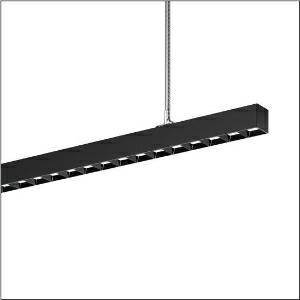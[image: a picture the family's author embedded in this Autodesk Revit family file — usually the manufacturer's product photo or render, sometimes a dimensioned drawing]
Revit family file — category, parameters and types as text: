
# Revit family: silica_r__21_51mx32dc4dbb_b922
name_source: partatom
category: Lighting Fixtures
units: mm (PartAtom-declared; Revit-internal decimal feet)

## family parameters
Cut with Voids When Loaded = No
Host = Face
Light Source = No
Part Type = Normal
Room Calculation Point = No
Round Connector Dimension = Use Diameter
Shared = No

## types (1)
- --- (1 x LED, 18230 lm, 105.8 W, 4000K)
    Apparent Load = 106 VA
    CIE Flux Codes = 86 99 100 59 100
    Color Rendering = 80
    Color Temperature = 4000K
    Default Elevation = 1800 mm
    Description = Silica® 21, office luminaire, primary light control with darklight reflector, of PMMA, black, CAT 2 (L<= 3000cd/m²), light emission: direct/indirect distribution, primary light characteristic: symmetric, installation type: suspended mounting, LED, rated luminous flux: 18.230lm, luminous efficacy: 172lm/W, light colour: 840, colour temperature: 4000K, control gear: DALI 2, with terminal, 3+2-pole, max. 2.5mm², mains connection: 220..240V, AC, 50/60Hz, rated input power: 105.8W, luminaire housing, of aluminium, matt jet black (RAL 9005), length: 3.004mm, width: 53mm, height: 53mm, protection rating (complete): IP20, insulation class (complete): insulation class I (protective earthing), certification: CE, permissible operating ambient temperature: 0..+35°C, standard: EN 50419, packaging unit: 1 piece
    Height = 53 mm
    Lamp = 1 x LED
    Lamp Light Flux = 18230 lm
    Lamp Power = 105.8 W
    Lamp count = 1
    Length = 3004 mm
    Luminous efficacy = 172 lm/W
    Manufacturer = Siteco
    ModVariant = No
    Model = 51MX32DC4DBB
    Mounting Place = Ceiling
    Mounting Type = Pendant
    Number of Poles = 1
    OnlyDefault = Yes
    Power Factor = 1
    Product Name = Silica® 21
    Product group = office luminaire | ceiling pendant
    ProductGroupID = 904
    Protection Class = Protection class I
    Protection Degree = IP 20
    RLX_Detail_Level = 1
    RLX_Emergency_Light_Flux = 0 lm
    RLX_Emergency_Type = 0
    RLX_Emergency_Type_DB = No
    RlxData = <blob elided: 66861 chars, md5=4f7c990a>
    Socket = socket
    Standby Power = 0 W
    System Light Flux = 18230 lm
    System Power = 106 W
    Type Comments = factory setting: luminous flux: 100 % | dim-lin: 254 | 366 mA
    Type Image = l_1335852.jpg
    URL = http://relux.com
    VarID = @adj_122110
    Voltage = 0 V
    Weight = 0.00 kg
    Width = 53 mm

## geometry (parser evidence)
native form markers: Blend x4, Sweep x13
no freeform markers — native parametric forms only
